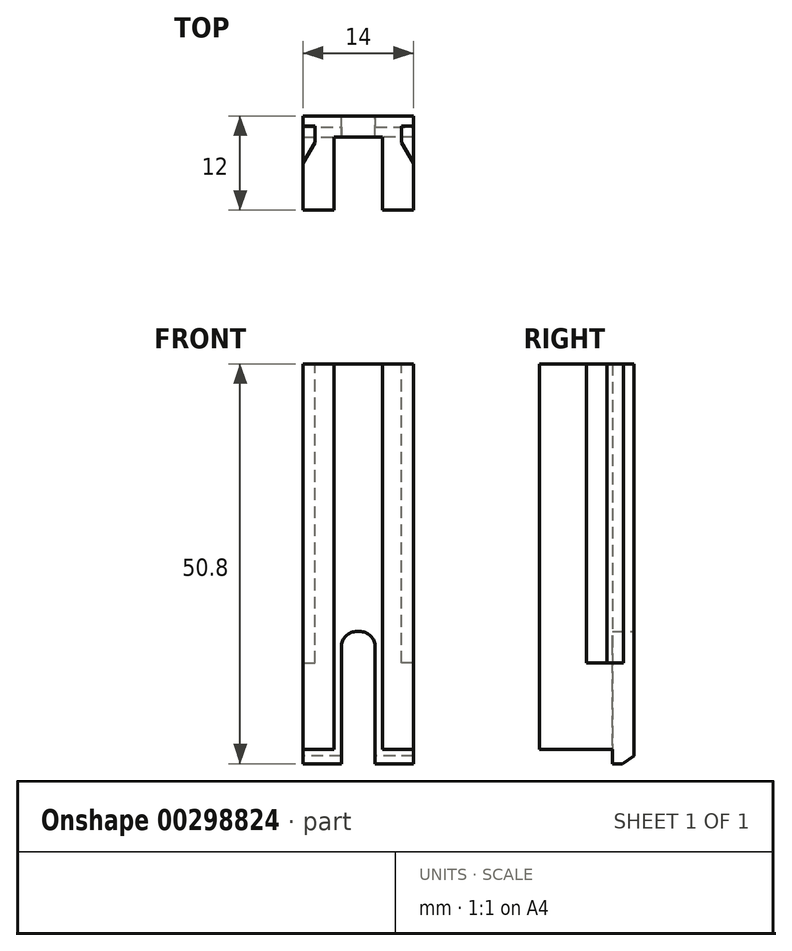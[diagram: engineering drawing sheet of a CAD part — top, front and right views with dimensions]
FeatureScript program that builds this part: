
annotation { "Feature Type Name" : "Feature", "Feature Type Description" : "" }
export const myFeature = defineFeature(function(context is Context, id is Id, definition is map)
    precondition{}
    {
        {
            var Q0;
            Q0=qCreatedBy(makeId("Top.planeOp"),FACE);
            var sketch = newSketch(context, id + "F0", { "sketchPlane" : qUnion([Q0])});
            skLineSegment(sketch, "E0", {"start": v(-3.08, 0) * mm, "end": v(-3.08, -9.3) * mm});
            skLineSegment(sketch, "E1", {"start": v(-3.07, -9.3) * mm, "end": v(-7, -9.3) * mm});
            skLineSegment(sketch, "E2", {"start": v(-7, -9.3) * mm, "end": v(-7, 2.7) * mm});
            skLineSegment(sketch, "E3", {"start": v(-7, 2.7) * mm, "end": v(0, 2.7) * mm});
            skLineSegment(sketch, "E4", {"start": v(-3.08, 0) * mm, "end": v(0, 0) * mm});
            skLineSegment(sketch, "E5.MirrorCS", {"start": v(7, -9.3) * mm, "end": v(7, 2.7) * mm});
            skLineSegment(sketch, "E6.MirrorCS", {"start": v(3.08, 0) * mm, "end": v(0, 0) * mm});
            skLineSegment(sketch, "E7.MirrorCS", {"start": v(3.08, 0) * mm, "end": v(3.08, -9.3) * mm});
            skLineSegment(sketch, "E8.MirrorCS", {"start": v(7, 2.7) * mm, "end": v(0, 2.7) * mm});
            skLineSegment(sketch, "E9.MirrorCS", {"start": v(3.07, -9.3) * mm, "end": v(7, -9.3) * mm});
            skSolve(sketch);
        }
        {
            var Q0;
            Q0=makeQuery(id+"F0.imprint","IMPRINT",FACE,{"disambiguationData":[TD([[makeQuery(id+"F0.imprint","IMPRINT",EDGE,{"derivedFrom":sQuery(id+"F0.wireOp",EDGE,"E0")}),-1.0]])]});
            extrude(context, id + "F1", {"entities" : qUnion([Q0]), "depth" : 49 * mm});
        }
        {
            var Q0;
            Q0=makeQuery(id+"F1.opExtrude","SWEPT_FACE",FACE,{"disambiguationData":[OSD([sQuery(id+"F0.wireOp",EDGE,"E3"),sQuery(id+"F0.wireOp",EDGE,"E8.MirrorCS")])]});
            var sketch = newSketch(context, id + "F2", { "sketchPlane" : qUnion([Q0])});
            skLineSegment(sketch, "E10.bottom", {"start": v(2.15, 0) * mm, "end": v(-2.15, 0) * mm});
            skLineSegment(sketch, "E10.top", {"start": v(2.15, 15) * mm, "end": v(-2.15, 15) * mm});
            skLineSegment(sketch, "E10.left", {"start": v(2.15, 0) * mm, "end": v(2.15, 15) * mm});
            skLineSegment(sketch, "E10.right", {"start": v(-2.15, 0) * mm, "end": v(-2.15, 15) * mm});
            skSolve(sketch);
        }
        {
            var Q0;
            Q0=makeQuery(id+"F2.imprint","IMPRINT",FACE,{"disambiguationData":[TD([[makeQuery(id+"F2.imprint","IMPRINT",EDGE,{"derivedFrom":sQuery(id+"F2.wireOp",EDGE,"E10.bottom")}),1.0]])]});
            extrude(context, id + "F3", {"entities" : qUnion([Q0]), "operationType" : NewBodyOperationType.REMOVE, "oppositeDirection" : true, "depth" : 25 * mm});
        }
        {
            var Q0;
            {var subQ0=sQuery(id+"F0.wireOp",EDGE,"E7.MirrorCS");var subQ1=sQuery(id+"F0.wireOp",EDGE,"E5.MirrorCS");var subQ2=sQuery(id+"F0.wireOp",EDGE,"E6.MirrorCS");var subQ3=sQuery(id+"F0.wireOp",EDGE,"E4");var subQ4=sQuery(id+"F0.wireOp",EDGE,"E8.MirrorCS");var subQ5=sQuery(id+"F0.wireOp",EDGE,"E3");var subQ6=sQuery(id+"F0.wireOp",EDGE,"E9.MirrorCS");Q0=makeQuery(id+"F3.boolean.opBoolean","SPLIT",FACE,{"disambiguationData":[TD([makeQuery(id+"F1.opExtrude","SWEPT_FACE",FACE,{"disambiguationData":[OSD([subQ1])]})])],"derivedFrom":makeQuery(id+"F1.opExtrude","CAP_FACE",FACE,{"disambiguationData":[OSD([sQuery(id+"F0.wireOp",EDGE,"E0"),sQuery(id+"F0.wireOp",EDGE,"E1"),sQuery(id+"F0.wireOp",EDGE,"E2"),subQ5,subQ3,subQ1,subQ2,subQ0,subQ4,subQ6])],"isStart":true})});}
            var sketch = newSketch(context, id + "F4", { "sketchPlane" : qUnion([Q0])});
            skLineSegment(sketch, "E11.bottom", {"start": v(7, -2.7) * mm, "end": v(2.15, -2.7) * mm});
            skLineSegment(sketch, "E11.top", {"start": v(7, 0) * mm, "end": v(2.15, 0) * mm});
            skLineSegment(sketch, "E11.left", {"start": v(7, -2.7) * mm, "end": v(7, 0) * mm});
            skLineSegment(sketch, "E11.right", {"start": v(2.15, -2.7) * mm, "end": v(2.15, 0) * mm});
            skLineSegment(sketch, "E12.MirrorCS", {"start": v(-7, -2.7) * mm, "end": v(-7, 0) * mm});
            skLineSegment(sketch, "E13.MirrorCS", {"start": v(-7, 0) * mm, "end": v(-2.15, 0) * mm});
            skLineSegment(sketch, "E14.MirrorCS", {"start": v(-2.15, -2.7) * mm, "end": v(-2.15, 0) * mm});
            skLineSegment(sketch, "E15.MirrorCS", {"start": v(-7, -2.7) * mm, "end": v(-2.15, -2.7) * mm});
            skSolve(sketch);
        }
        {
            var Q0;
            Q0=makeQuery(id+"F4.imprint","IMPRINT",FACE,{"disambiguationData":[TD([[makeQuery(id+"F4.imprint","IMPRINT",EDGE,{"derivedFrom":sQuery(id+"F4.wireOp",EDGE,"E11.bottom")}),-1.0]])]});
            var Q1;
            Q1=makeQuery(id+"F4.imprint","IMPRINT",FACE,{"disambiguationData":[TD([[makeQuery(id+"F4.imprint","IMPRINT",EDGE,{"derivedFrom":sQuery(id+"F4.wireOp",EDGE,"E12.MirrorCS")}),-1.0]])]});
            extrude(context, id + "F5", {"entities" : qUnion([Q0, Q1]), "operationType" : NewBodyOperationType.ADD, "depth" : 1.8 * mm});
        }
        {
            var Q0;
            Q0=makeQuery(id+"F3.boolean.opBoolean","COPY",EDGE,{"derivedFrom":makeQuery(id+"F3.opExtrude","SWEPT_EDGE",EDGE,{"disambiguationData":[OSD([sQuery(id+"F2.wireOp",EDGE,"E10.top"),sQuery(id+"F2.wireOp",EDGE,"E10.right")])]})});
            var Q1;
            Q1=makeQuery(id+"F3.boolean.opBoolean","COPY",EDGE,{"derivedFrom":makeQuery(id+"F3.opExtrude","SWEPT_EDGE",EDGE,{"disambiguationData":[OSD([sQuery(id+"F2.wireOp",EDGE,"E10.top"),sQuery(id+"F2.wireOp",EDGE,"E10.left")])]})});
            fillet(context, id + "F6", {"entities" : qUnion([Q0, Q1]), "radius" : 2 * mm, "tangentPropagation" : true, "allowEdgeOverflow" : false});
        }
        {
            var Q0;
            Q0=makeQuery(id+"F5.opExtrude","CAP_EDGE",EDGE,{"disambiguationData":[OSD([sQuery(id+"F4.wireOp",EDGE,"E11.bottom")])],"isStart":false});
            var Q1;
            Q1=makeQuery(id+"F5.opExtrude","CAP_EDGE",EDGE,{"disambiguationData":[OSD([sQuery(id+"F4.wireOp",EDGE,"E15.MirrorCS")])],"isStart":false});
            chamfer(context, id + "F7", {"entities" : qUnion([Q0, Q1]), "chamferType" : ChamferType.OFFSET_ANGLE, "width" : 1 * mm, "oppositeDirection" : false, "angle" : 55 * degree, "tangentPropagation" : true});
        }
        {
            var Q0;
            Q0=makeQuery(id+"F1.opExtrude","CAP_FACE",FACE,{"disambiguationData":[OSD([sQuery(id+"F0.wireOp",EDGE,"E0"),sQuery(id+"F0.wireOp",EDGE,"E1"),sQuery(id+"F0.wireOp",EDGE,"E2"),sQuery(id+"F0.wireOp",EDGE,"E3"),sQuery(id+"F0.wireOp",EDGE,"E4"),sQuery(id+"F0.wireOp",EDGE,"E5.MirrorCS"),sQuery(id+"F0.wireOp",EDGE,"E6.MirrorCS"),sQuery(id+"F0.wireOp",EDGE,"E7.MirrorCS"),sQuery(id+"F0.wireOp",EDGE,"E8.MirrorCS"),sQuery(id+"F0.wireOp",EDGE,"E9.MirrorCS")])],"isStart":false});
            var sketch = newSketch(context, id + "F8", { "sketchPlane" : qUnion([Q0])});
            skLineSegment(sketch, "E16", {"start": v(-7, 1.4) * mm, "end": v(-5.5, 1.4) * mm});
            skLineSegment(sketch, "E17", {"start": v(-5.5, 1.4) * mm, "end": v(-5.5, -0.7) * mm});
            skLineSegment(sketch, "E18", {"start": v(-5.5, -0.7) * mm, "end": v(-7, -3.3) * mm});
            skLineSegment(sketch, "E19", {"start": v(-7, -3.3) * mm, "end": v(-7, 1.4) * mm});
            skLineSegment(sketch, "E20.MirrorCS", {"start": v(7, 1.4) * mm, "end": v(5.5, 1.4) * mm});
            skLineSegment(sketch, "E21.MirrorCS", {"start": v(5.5, 1.4) * mm, "end": v(5.5, -0.7) * mm});
            skLineSegment(sketch, "E22.MirrorCS", {"start": v(7, -3.3) * mm, "end": v(7, 1.4) * mm});
            skLineSegment(sketch, "E23.MirrorCS", {"start": v(5.5, -0.7) * mm, "end": v(7, -3.3) * mm});
            skSolve(sketch);
        }
        {
            var Q0;
            Q0=makeQuery(id+"F8.imprint","IMPRINT",FACE,{"disambiguationData":[TD([[makeQuery(id+"F8.imprint","IMPRINT",EDGE,{"derivedFrom":sQuery(id+"F8.wireOp",EDGE,"E20.MirrorCS")}),1.0]])]});
            var Q1;
            Q1=makeQuery(id+"F8.imprint","IMPRINT",FACE,{"disambiguationData":[TD([[makeQuery(id+"F8.imprint","IMPRINT",EDGE,{"derivedFrom":sQuery(id+"F8.wireOp",EDGE,"E16")}),-1.0]])]});
            extrude(context, id + "F9", {"entities" : qUnion([Q0, Q1]), "operationType" : NewBodyOperationType.REMOVE, "oppositeDirection" : true, "depth" : 38 * mm});
        }
    });
